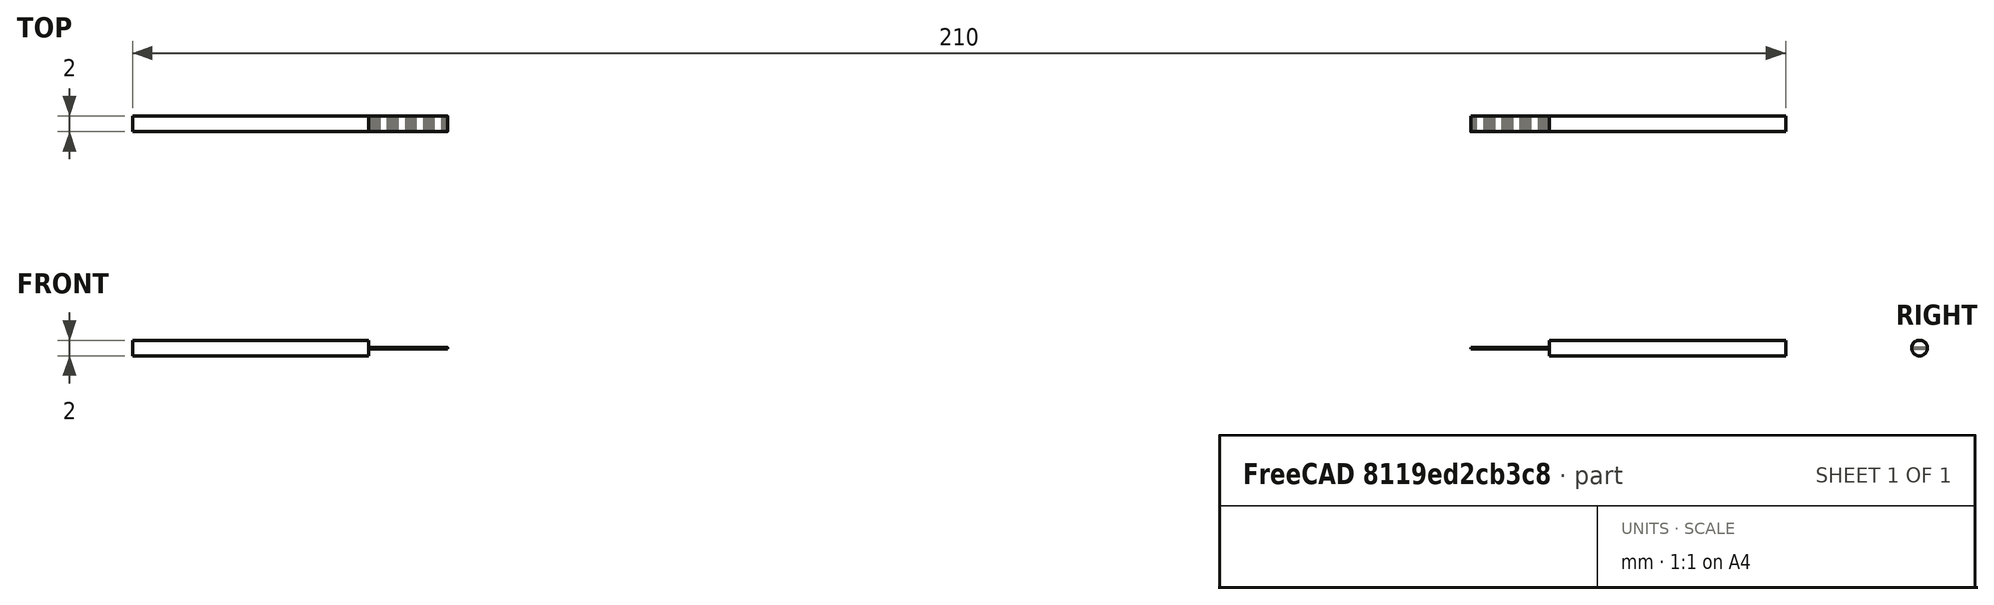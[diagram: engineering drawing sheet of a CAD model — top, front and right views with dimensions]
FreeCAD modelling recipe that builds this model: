
FCSTD DOCUMENT  (FreeCAD 0.15R4671 (Git))
Label: bend sensor diagram
License: All rights reserved
LicenseURL: http://en.wikipedia.org/wiki/All_rights_reserved
objects: Part::Cylinder×42, Part::Part2DObjectPython×4, Part::Compound×2, App::DocumentObjectGroup×1
note: 48 computed .brp shape members not serialized (recipe doc carries the construction recipe); baked Part::Feature solids carry a one-line shape summary decoded from their .brp

FEATURE [Part::Part2DObjectPython] Rectangle  # Draft 2D object (typed FeaturePython)
  ChamferSize = 0
  FilletRadius = 0
  Height = 15
  Length = 150
  MakeFace = true
FEATURE [Part::Part2DObjectPython] Rectangle001  # Draft 2D object (typed FeaturePython)
  ChamferSize = 0
  FilletRadius = 0
  Height = 140
  Length = 12
  MakeFace = true
  Placement = pos=(5,1.5,10) rot=(0.707107,0.707107,0;3.14159rad)
FEATURE [Part::Part2DObjectPython] Rectangle002  # Draft 2D object (typed FeaturePython)
  ChamferSize = 0
  FilletRadius = 0
  Height = 8
  Length = 140
  MakeFace = true
  Placement = pos=(5,3.5,15) rot=(0,0,1;0rad)
FEATURE [Part::Part2DObjectPython] Rectangle003  # Draft 2D object (typed FeaturePython)
  ChamferSize = 0
  FilletRadius = 0
  Height = 4
  Length = 140
  MakeFace = true
  Placement = pos=(5,5.5,20) rot=(0,0,1;0rad)
FEATURE [Part::Cylinder] Cylinder
  Angle = 360
  Height = 30
  Placement = pos=(-30,7.5,1) rot=(0,1,0;1.5708rad)
  Radius = 1
FEATURE [Part::Cylinder] Cylinder001
  Angle = 360
  Height = 10
  Placement = pos=(0,6.6,1) rot=(0,1,0;1.5708rad)
  Radius = 0.1
FEATURE [Part::Cylinder] Cylinder002
  Angle = 360
  Height = 10
  Placement = pos=(0,6.6,1) rot=(0,1,0;1.5708rad)
  Radius = 0.1
FEATURE [Part::Cylinder] Cylinder003
  Angle = 360
  Height = 10
  Placement = pos=(0,6.7,1) rot=(0,1,0;1.5708rad)
  Radius = 0.1
FEATURE [Part::Cylinder] Cylinder004
  Angle = 360
  Height = 10
  Placement = pos=(0,6.8,1) rot=(0,1,0;1.5708rad)
  Radius = 0.1
FEATURE [Part::Cylinder] Cylinder005
  Angle = 360
  Height = 10
  Placement = pos=(0,6.9,1) rot=(0,1,0;1.5708rad)
  Radius = 0.1
FEATURE [Part::Cylinder] Cylinder006
  Angle = 360
  Height = 10
  Placement = pos=(0,7,1) rot=(0,1,0;1.5708rad)
  Radius = 0.1
FEATURE [Part::Cylinder] Cylinder007
  Angle = 360
  Height = 10
  Placement = pos=(0,7.1,1) rot=(0,1,0;1.5708rad)
  Radius = 0.1
FEATURE [Part::Cylinder] Cylinder008
  Angle = 360
  Height = 10
  Placement = pos=(0,7.2,1) rot=(0,1,0;1.5708rad)
  Radius = 0.1
FEATURE [Part::Cylinder] Cylinder009
  Angle = 360
  Height = 10
  Placement = pos=(0,7.3,1) rot=(0,1,0;1.5708rad)
  Radius = 0.1
FEATURE [Part::Cylinder] Cylinder010
  Angle = 360
  Height = 10
  Placement = pos=(0,7.4,1) rot=(0,1,0;1.5708rad)
  Radius = 0.1
FEATURE [Part::Cylinder] Cylinder011
  Angle = 360
  Height = 10
  Placement = pos=(0,7.5,1) rot=(0,1,0;1.5708rad)
  Radius = 0.1
FEATURE [Part::Cylinder] Cylinder012
  Angle = 360
  Height = 10
  Placement = pos=(0,7.6,1) rot=(0,1,0;1.5708rad)
  Radius = 0.1
FEATURE [Part::Cylinder] Cylinder013
  Angle = 360
  Height = 10
  Placement = pos=(0,7.7,1) rot=(0,1,0;1.5708rad)
  Radius = 0.1
FEATURE [Part::Cylinder] Cylinder014
  Angle = 360
  Height = 10
  Placement = pos=(0,7.8,1) rot=(0,1,0;1.5708rad)
  Radius = 0.1
FEATURE [Part::Cylinder] Cylinder015
  Angle = 360
  Height = 10
  Placement = pos=(0,7.9,1) rot=(0,1,0;1.5708rad)
  Radius = 0.1
FEATURE [Part::Cylinder] Cylinder016
  Angle = 360
  Height = 10
  Placement = pos=(0,8,1) rot=(0,1,0;1.5708rad)
  Radius = 0.1
FEATURE [Part::Cylinder] Cylinder017
  Angle = 360
  Height = 10
  Placement = pos=(0,8.1,1) rot=(0,1,0;1.5708rad)
  Radius = 0.1
FEATURE [Part::Cylinder] Cylinder018
  Angle = 360
  Height = 10
  Placement = pos=(0,8.2,1) rot=(0,1,0;1.5708rad)
  Radius = 0.1
FEATURE [Part::Cylinder] Cylinder019
  Angle = 360
  Height = 10
  Placement = pos=(0,8.3,1) rot=(0,1,0;1.5708rad)
  Radius = 0.1
FEATURE [Part::Cylinder] Cylinder020
  Angle = 360
  Height = 10
  Placement = pos=(0,8.4,1) rot=(0,1,0;1.5708rad)
  Radius = 0.1
FEATURE [App::DocumentObjectGroup] Group  label="wire"
  Group = -> [Cylinder,Cylinder001,Cylinder002,Cylinder003,Cylinder004,Cylinder005,Cylinder006,Cylinder007,Cylinder008,Cylinder009,Cylinder010,Cylinder011,Cylinder012,Cylinder013,Cylinder014,Cylinder015,Cylinder016,Cylinder017,Cylinder018,Cylinder019,Cylinder020]
FEATURE [Part::Compound] Compound
  Links = -> [Cylinder,Cylinder001,Cylinder019,Cylinder007,Cylinder008,Cylinder003,Cylinder002,Cylinder005,Cylinder004,Cylinder006,Cylinder015,Cylinder014,Cylinder011,Cylinder012,Cylinder013,Cylinder010,Cylinder017,Cylinder009,Cylinder020,Cylinder016,Cylinder018]
  Placement = pos=(150,15,0) rot=(0,0,1;3.14159rad)
FEATURE [Part::Cylinder] Cylinder021
  Angle = 360
  Height = 30
  Placement = pos=(-30,7.5,1) rot=(0,1,0;1.5708rad)
  Radius = 1
FEATURE [Part::Cylinder] Cylinder022
  Angle = 360
  Height = 10
  Placement = pos=(0,6.6,1) rot=(0,1,0;1.5708rad)
  Radius = 0.1
FEATURE [Part::Cylinder] Cylinder023
  Angle = 360
  Height = 10
  Placement = pos=(0,6.6,1) rot=(0,1,0;1.5708rad)
  Radius = 0.1
FEATURE [Part::Cylinder] Cylinder024
  Angle = 360
  Height = 10
  Placement = pos=(0,6.7,1) rot=(0,1,0;1.5708rad)
  Radius = 0.1
FEATURE [Part::Cylinder] Cylinder025
  Angle = 360
  Height = 10
  Placement = pos=(0,6.8,1) rot=(0,1,0;1.5708rad)
  Radius = 0.1
FEATURE [Part::Cylinder] Cylinder026
  Angle = 360
  Height = 10
  Placement = pos=(0,6.9,1) rot=(0,1,0;1.5708rad)
  Radius = 0.1
FEATURE [Part::Cylinder] Cylinder027
  Angle = 360
  Height = 10
  Placement = pos=(0,7,1) rot=(0,1,0;1.5708rad)
  Radius = 0.1
FEATURE [Part::Cylinder] Cylinder028
  Angle = 360
  Height = 10
  Placement = pos=(0,7.1,1) rot=(0,1,0;1.5708rad)
  Radius = 0.1
FEATURE [Part::Cylinder] Cylinder029
  Angle = 360
  Height = 10
  Placement = pos=(0,7.2,1) rot=(0,1,0;1.5708rad)
  Radius = 0.1
FEATURE [Part::Cylinder] Cylinder030
  Angle = 360
  Height = 10
  Placement = pos=(0,7.3,1) rot=(0,1,0;1.5708rad)
  Radius = 0.1
FEATURE [Part::Cylinder] Cylinder031
  Angle = 360
  Height = 10
  Placement = pos=(0,7.4,1) rot=(0,1,0;1.5708rad)
  Radius = 0.1
FEATURE [Part::Cylinder] Cylinder032
  Angle = 360
  Height = 10
  Placement = pos=(0,7.5,1) rot=(0,1,0;1.5708rad)
  Radius = 0.1
FEATURE [Part::Cylinder] Cylinder033
  Angle = 360
  Height = 10
  Placement = pos=(0,7.6,1) rot=(0,1,0;1.5708rad)
  Radius = 0.1
FEATURE [Part::Cylinder] Cylinder034
  Angle = 360
  Height = 10
  Placement = pos=(0,7.7,1) rot=(0,1,0;1.5708rad)
  Radius = 0.1
FEATURE [Part::Cylinder] Cylinder035
  Angle = 360
  Height = 10
  Placement = pos=(0,7.8,1) rot=(0,1,0;1.5708rad)
  Radius = 0.1
FEATURE [Part::Cylinder] Cylinder036
  Angle = 360
  Height = 10
  Placement = pos=(0,7.9,1) rot=(0,1,0;1.5708rad)
  Radius = 0.1
FEATURE [Part::Cylinder] Cylinder037
  Angle = 360
  Height = 10
  Placement = pos=(0,8,1) rot=(0,1,0;1.5708rad)
  Radius = 0.1
FEATURE [Part::Cylinder] Cylinder038
  Angle = 360
  Height = 10
  Placement = pos=(0,8.1,1) rot=(0,1,0;1.5708rad)
  Radius = 0.1
FEATURE [Part::Cylinder] Cylinder039
  Angle = 360
  Height = 10
  Placement = pos=(0,8.2,1) rot=(0,1,0;1.5708rad)
  Radius = 0.1
FEATURE [Part::Cylinder] Cylinder040
  Angle = 360
  Height = 10
  Placement = pos=(0,8.3,1) rot=(0,1,0;1.5708rad)
  Radius = 0.1
FEATURE [Part::Cylinder] Cylinder041
  Angle = 360
  Height = 10
  Placement = pos=(0,8.4,1) rot=(0,1,0;1.5708rad)
  Radius = 0.1
FEATURE [Part::Compound] Compound001
  Links = -> [Cylinder021,Cylinder022,Cylinder040,Cylinder028,Cylinder029,Cylinder024,Cylinder023,Cylinder026,Cylinder025,Cylinder027,Cylinder036,Cylinder035,Cylinder032,Cylinder033,Cylinder034,Cylinder031,Cylinder038,Cylinder030,Cylinder041,Cylinder037,Cylinder039]
